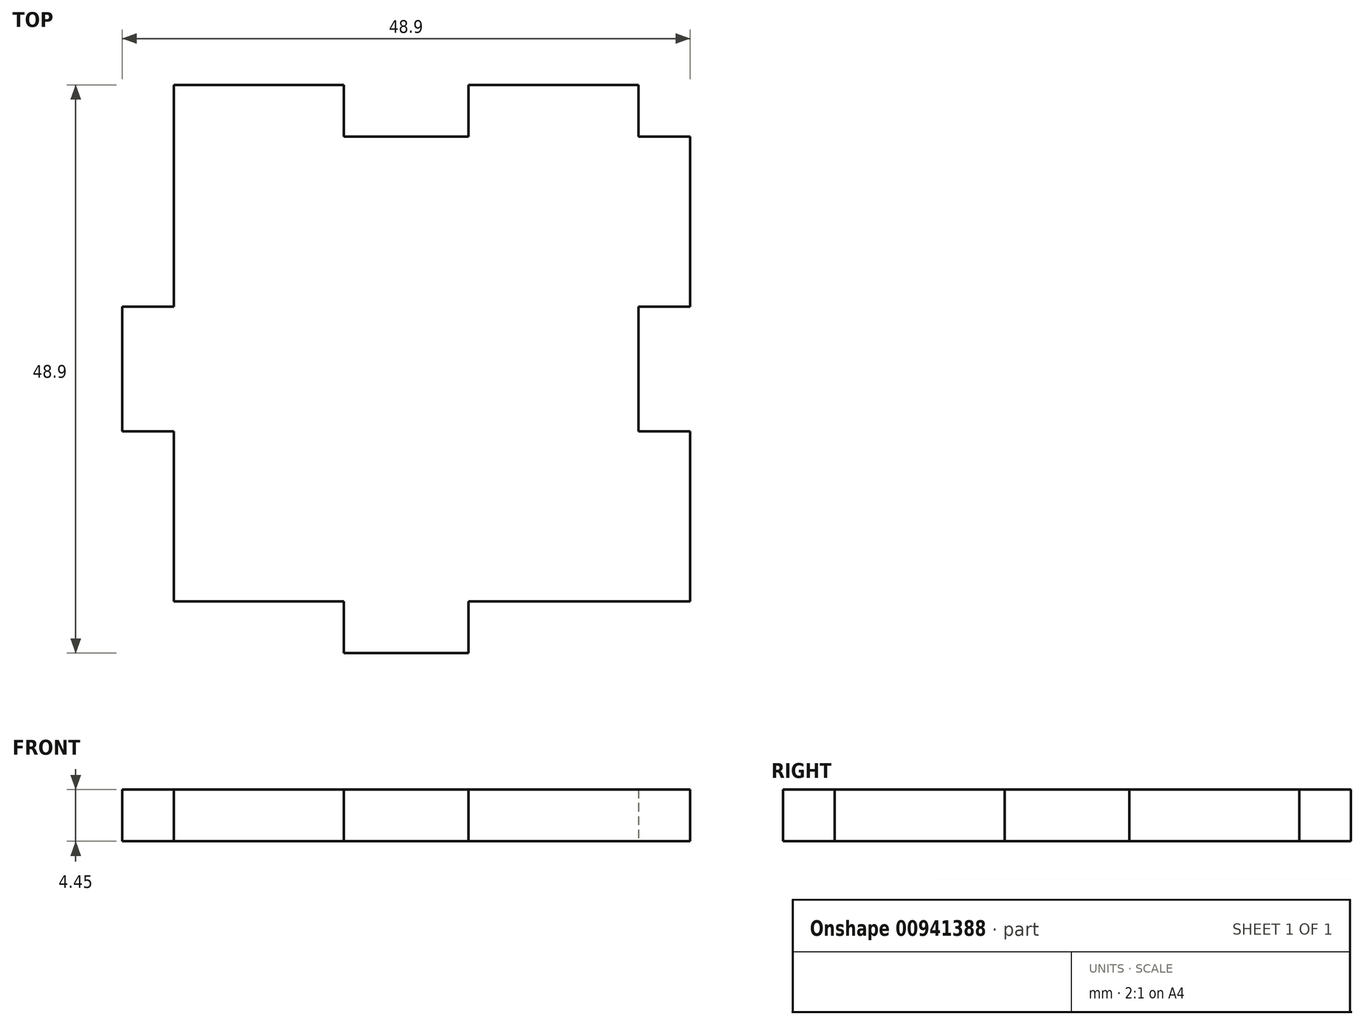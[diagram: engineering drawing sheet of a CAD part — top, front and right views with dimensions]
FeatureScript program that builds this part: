
annotation { "Feature Type Name" : "Feature", "Feature Type Description" : "" }
export const myFeature = defineFeature(function(context is Context, id is Id, definition is map)
    precondition{}
    {
        {
            var Q0;
            Q0=qCreatedBy(makeId("Top.planeOp"),FACE);
            var sketch = newSketch(context, id + "F0", { "sketchPlane" : qUnion([Q0])});
            skLineSegment(sketch, "E0.bottom", {"start": v(20, -20) * mm, "end": v(5.36, -20) * mm});
            skLineSegment(sketch, "E0.top", {"start": v(5.36, 20) * mm, "end": v(-5.36, 20) * mm});
            skLineSegment(sketch, "E0.right", {"start": v(-20, -20) * mm, "end": v(-20, -5.36) * mm});
            skPoint(sketch, "E0.middle", {"position": v(0, 0) * mm});
            skLineSegment(sketch, "E1.bottom", {"start": v(-24.45, -5.36) * mm, "end": v(-20, -5.36) * mm});
            skLineSegment(sketch, "E1.top", {"start": v(-24.45, 5.36) * mm, "end": v(-20, 5.36) * mm});
            skLineSegment(sketch, "E1.left", {"start": v(-24.45, -5.36) * mm, "end": v(-24.45, 5.36) * mm});
            skLineSegment(sketch, "E2.trimOffspring", {"start": v(20, 5.36) * mm, "end": v(24.45, 5.36) * mm});
            skLineSegment(sketch, "E3.trimOffspring", {"start": v(20, -5.36) * mm, "end": v(24.45, -5.36) * mm});
            skLineSegment(sketch, "E4.bottom", {"start": v(20, 20) * mm, "end": v(24.45, 20) * mm});
            skLineSegment(sketch, "E4.right", {"start": v(24.45, 20) * mm, "end": v(24.45, 5.36) * mm});
            skLineSegment(sketch, "E5.top", {"start": v(20, -20) * mm, "end": v(24.45, -20) * mm});
            skLineSegment(sketch, "E5.right", {"start": v(24.45, -5.36) * mm, "end": v(24.45, -20) * mm});
            skLineSegment(sketch, "E6.trimOffspring", {"start": v(-20, 5.36) * mm, "end": v(-20, 20) * mm});
            skLineSegment(sketch, "E7", {"start": v(20, 5.36) * mm, "end": v(20, -5.36) * mm});
            skLineSegment(sketch, "E8.top", {"start": v(-20, 20) * mm, "end": v(-20, 5.36) * mm});
            skLineSegment(sketch, "E9.bottom", {"start": v(5.36, -24.45) * mm, "end": v(5.36, -20) * mm});
            skLineSegment(sketch, "E9.top", {"start": v(-5.36, -24.45) * mm, "end": v(-5.36, -20) * mm});
            skLineSegment(sketch, "E9.left", {"start": v(5.36, -24.45) * mm, "end": v(-5.36, -24.45) * mm});
            skLineSegment(sketch, "E10.trimOffspring", {"start": v(-5.36, 20) * mm, "end": v(-5.36, 24.45) * mm});
            skLineSegment(sketch, "E11.trimOffspring", {"start": v(5.36, 20) * mm, "end": v(5.36, 24.45) * mm});
            skLineSegment(sketch, "E12.bottom", {"start": v(-20, 20) * mm, "end": v(-20, 24.45) * mm});
            skLineSegment(sketch, "E12.right", {"start": v(-20, 24.45) * mm, "end": v(-5.36, 24.45) * mm});
            skLineSegment(sketch, "E13.top", {"start": v(20, 20) * mm, "end": v(20, 24.45) * mm});
            skLineSegment(sketch, "E13.right", {"start": v(5.36, 24.45) * mm, "end": v(20, 24.45) * mm});
            skLineSegment(sketch, "E14.trimOffspring", {"start": v(-5.36, -20) * mm, "end": v(-20, -20) * mm});
            skLineSegment(sketch, "E15", {"start": v(-5.36, 20) * mm, "end": v(5.36, 20) * mm});
            skPoint(sketch, "E16.orphan", {"position": v(20, 20) * mm});
            skLineSegment(sketch, "E17.trimOffspring", {"start": v(-20, -5.36) * mm, "end": v(-20, -20) * mm});
            skSolve(sketch);
        }
        {
            var Q0;
            Q0=makeQuery(id+"F0.imprint","IMPRINT",FACE,{"disambiguationData":[TD([[makeQuery(id+"F0.imprint","IMPRINT",EDGE,{"derivedFrom":sQuery(id+"F0.wireOp",EDGE,"E1.bottom")}),1.0]])]});
            extrude(context, id + "F1", {"entities" : qUnion([Q0]), "depth" : 4.45 * mm, "offsetDistance" : 25 * mm});
        }
    });
